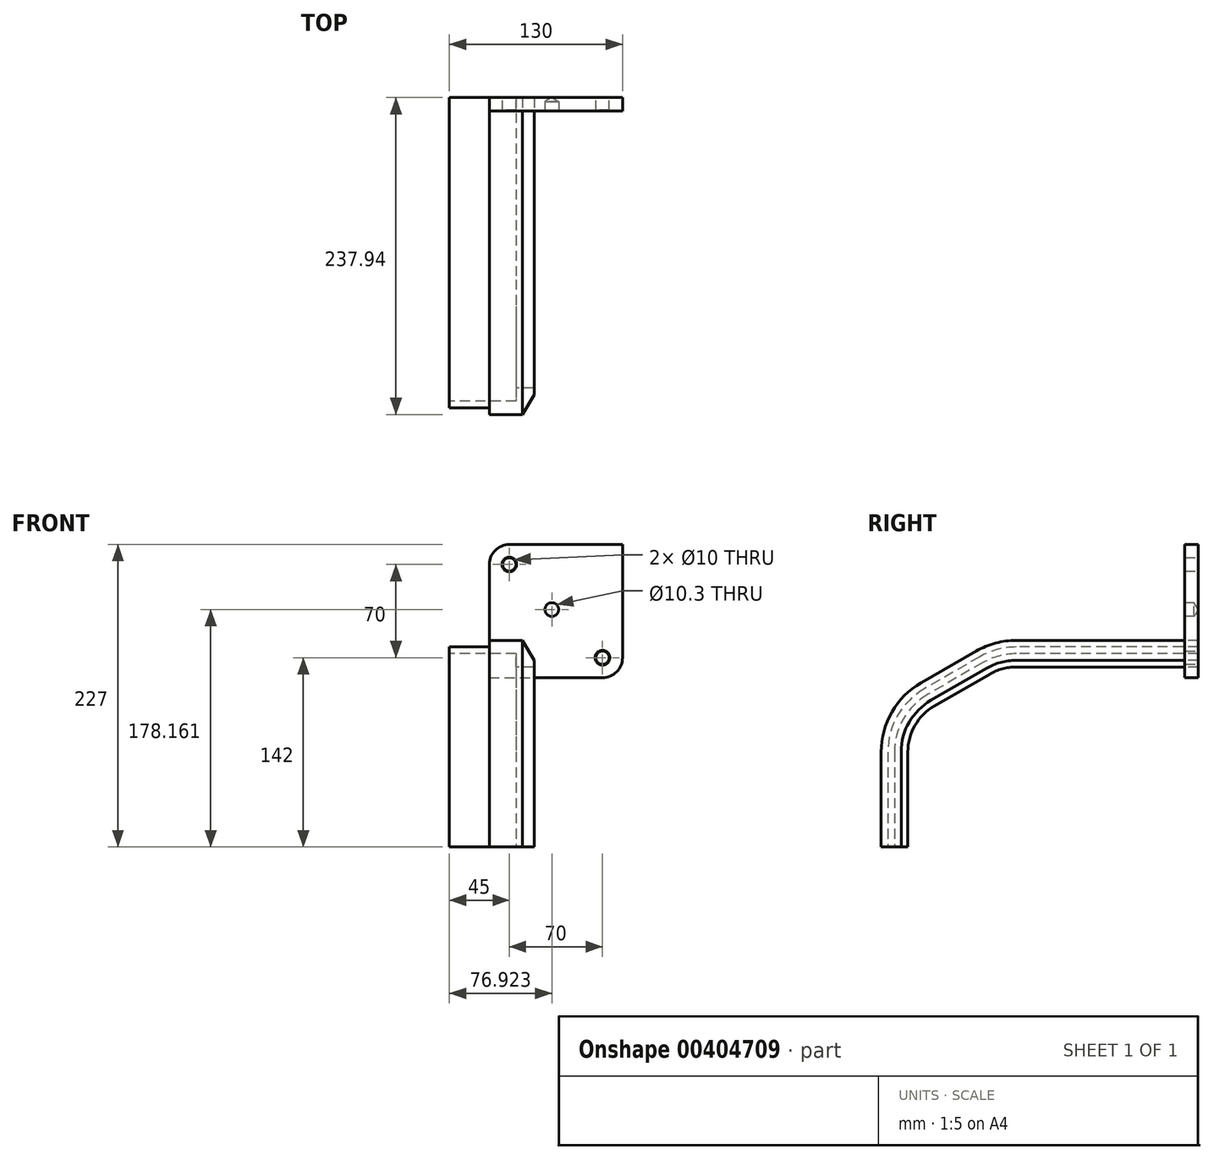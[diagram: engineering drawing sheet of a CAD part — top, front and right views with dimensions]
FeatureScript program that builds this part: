
annotation { "Feature Type Name" : "Feature", "Feature Type Description" : "" }
export const myFeature = defineFeature(function(context is Context, id is Id, definition is map)
    precondition{}
    {
        {
            var Q0;
            Q0=qCreatedBy(makeId("Front.planeOp"),FACE);
            var sketch = newSketch(context, id + "F0", { "sketchPlane" : qUnion([Q0])});
            skLineSegment(sketch, "E0.bottom", {"start": v(0, 0) * mm, "end": v(85, 0) * mm});
            skLineSegment(sketch, "E0.top", {"start": v(15, 100) * mm, "end": v(100, 100) * mm});
            skLineSegment(sketch, "E0.left", {"start": v(0, 0) * mm, "end": v(0, 85) * mm});
            skLineSegment(sketch, "E0.right", {"start": v(100, 15) * mm, "end": v(100, 100) * mm});
            skPoint(sketch, "E1.visualSharp", {"position": v(0, 100) * mm});
            skArc(sketch, "E1.filletArc", {"start": v(15, 100) * mm, "mid": v(4.4, 95.6) * mm, "end": v(0, 85) * mm});
            skPoint(sketch, "E2.visualSharp", {"position": v(100, 0) * mm});
            skArc(sketch, "E2.filletArc", {"start": v(85, 0) * mm, "mid": v(95.6, 4.4) * mm, "end": v(100, 15) * mm});
            skCircle(sketch, "E3", {"center": v(15, 85) * mm, "radius": 5 * mm});
            skCircle(sketch, "E4", {"center": v(85, 15) * mm, "radius": 5 * mm});
            skSolve(sketch);
        }
        {
            var Q0;
            Q0=makeQuery(id+"F0.imprint","IMPRINT",FACE,{"disambiguationData":[TD([[makeQuery(id+"F0.imprint","IMPRINT",EDGE,{"derivedFrom":sQuery(id+"F0.wireOp",EDGE,"E0.bottom")}),1.0]])]});
            extrude(context, id + "F1", {"entities" : qUnion([Q0]), "depth" : 10 * mm});
        }
        {
            var Q0;
            Q0=makeQuery(id+"F1.opExtrude","CAP_FACE",FACE,{"disambiguationData":[OSD([sQuery(id+"F0.wireOp",EDGE,"E0.bottom"),sQuery(id+"F0.wireOp",EDGE,"E0.top"),sQuery(id+"F0.wireOp",EDGE,"E0.left"),sQuery(id+"F0.wireOp",EDGE,"E0.right"),sQuery(id+"F0.wireOp",EDGE,"E1.filletArc"),sQuery(id+"F0.wireOp",EDGE,"E2.filletArc"),sQuery(id+"F0.wireOp",EDGE,"E3"),sQuery(id+"F0.wireOp",EDGE,"E4")])],"isStart":false});
            var sketch = newSketch(context, id + "F2", { "sketchPlane" : qUnion([Q0])});
            skPoint(sketch, "E5", {"position": v(46.92, 51.16) * mm});
            skSolve(sketch);
        }
        {
            var Q0;
            Q0=sQuery(id+"F2.wireOp",VERTEX,"E5");
            var Q1;
            Q1=makeQuery(id+"F1.opExtrude","SWEPT_BODY",BODY,{"disambiguationData":[OSD([sQuery(id+"F0.wireOp",EDGE,"E0.bottom"),sQuery(id+"F0.wireOp",EDGE,"E0.top"),sQuery(id+"F0.wireOp",EDGE,"E0.left"),sQuery(id+"F0.wireOp",EDGE,"E0.right"),sQuery(id+"F0.wireOp",EDGE,"E1.filletArc"),sQuery(id+"F0.wireOp",EDGE,"E2.filletArc"),sQuery(id+"F0.wireOp",EDGE,"E3"),sQuery(id+"F0.wireOp",EDGE,"E4")])]});
            hole(context, id + "F3", {"style" : HoleStyle.SIMPLE, "endStyle" : HoleEndStyle.BLIND, "standardTappedOrClearance" : lookupTablePath({ "standard" : "ISO", "engagement" : "75%", "pitch" : "1.75 mm", "size" : "M12", "type" : "Tapped" }), "standardBlindInLast" : lookupTablePath({ "standard" : "ISO", "engagement" : "75%", "pitch" : "1.75 mm", "size" : "M12", "type" : "Tapped" }), "holeDiameter" : 10.3 * mm, "showTappedDepth" : true, "holeDepth" : 7 * mm, "isTappedThrough" : true, "tappedDepth" : 1.75 * mm, "tapClearance" : 3, "locations" : qUnion([Q0]), "scope" : qUnion([Q1]), "majorDiameter" : 12 * mm});
        }
        {
            var Q0;
            Q0=makeQuery(id+"F3.hole-0.boolean.opBoolean","COPY",EDGE,{"derivedFrom":makeQuery(id+"F3.hole-0.opRevolve","SWEPT_EDGE",EDGE,{"disambiguationData":[OSD([sQuery(id+"F3.hole-0.sketch.wireOp",EDGE,"core_line_2"),sQuery(id+"F3.hole-0.sketch.wireOp",EDGE,"core_line_3")])]})});
            var Q1;
            Q1=makeQuery(id+"F1.opExtrude","CAP_EDGE",EDGE,{"disambiguationData":[OSD([sQuery(id+"F0.wireOp",EDGE,"E3")])],"isStart":false});
            var Q2;
            Q2=makeQuery(id+"F1.opExtrude","CAP_EDGE",EDGE,{"disambiguationData":[OSD([sQuery(id+"F0.wireOp",EDGE,"E4")])],"isStart":false});
            chamfer(context, id + "F4", {"entities" : qUnion([Q0, Q1, Q2]), "width" : 0.5 * mm, "tangentPropagation" : true});
        }
        {
            var Q0;
            Q0=qCreatedBy(makeId("Front.planeOp"),FACE);
            var sketch = newSketch(context, id + "F5", { "sketchPlane" : qUnion([Q0])});
            skLineSegment(sketch, "E6", {"start": v(-30, 18) * mm, "end": v(-30, 23) * mm});
            skLineSegment(sketch, "E7", {"start": v(-30, 23) * mm, "end": v(0, 23) * mm});
            skLineSegment(sketch, "E8", {"start": v(0, 23) * mm, "end": v(0, 28) * mm});
            skLineSegment(sketch, "E9", {"start": v(0, 28) * mm, "end": v(25, 28) * mm});
            skLineSegment(sketch, "E10", {"start": v(25, 28) * mm, "end": v(33.66, 13) * mm});
            skLineSegment(sketch, "E11", {"start": v(33.66, 13) * mm, "end": v(33.66, 8) * mm});
            skLineSegment(sketch, "E12", {"start": v(33.66, 8) * mm, "end": v(20, 8) * mm});
            skLineSegment(sketch, "E13", {"start": v(20, 8) * mm, "end": v(20, 18) * mm});
            skLineSegment(sketch, "E14", {"start": v(20, 18) * mm, "end": v(-30, 18) * mm});
            skLineSegment(sketch, "E15", {"start": v(0, 0) * mm, "end": v(-60.46, 0) * mm, "construction": true});
            skSolve(sketch);
        }
        {
            var Q0;
            Q0=qCreatedBy(makeId("Right.planeOp"),FACE);
            var sketch = newSketch(context, id + "F6", { "sketchPlane" : qUnion([Q0])});
            skPoint(sketch, "E16.0", {"position": v(0, 18) * mm});
            skLineSegment(sketch, "E17", {"start": v(0, 18) * mm, "end": v(-136.6, 18) * mm});
            skLineSegment(sketch, "E18", {"start": v(-161.6, 11.3) * mm, "end": v(-202.94, -12.57) * mm});
            skLineSegment(sketch, "E19", {"start": v(-227.94, -55.87) * mm, "end": v(-227.94, -127) * mm});
            skPoint(sketch, "E20.visualSharp", {"position": v(-150, 18) * mm});
            skArc(sketch, "E20.filletArc", {"start": v(-136.6, 18) * mm, "mid": v(-149.54, 16.3) * mm, "end": v(-161.6, 11.3) * mm});
            skPoint(sketch, "E21.visualSharp", {"position": v(-227.94, -27) * mm});
            skArc(sketch, "E21.filletArc", {"start": v(-202.94, -12.57) * mm, "mid": v(-221.24, -30.87) * mm, "end": v(-227.94, -55.87) * mm});
            skSolve(sketch);
        }
        {
            var Q0;
            Q0=makeQuery(id+"F5.imprint","IMPRINT",FACE,{"disambiguationData":[TD([[makeQuery(id+"F5.imprint","IMPRINT",EDGE,{"derivedFrom":sQuery(id+"F5.wireOp",EDGE,"E6")}),-1.0]])]});
            var Q1;
            Q1=sQuery(id+"F6.wireOp",EDGE,"E17");
            var Q2;
            Q2=sQuery(id+"F6.wireOp",EDGE,"E20.filletArc");
            var Q3;
            Q3=sQuery(id+"F6.wireOp",EDGE,"E18");
            var Q4;
            Q4=sQuery(id+"F6.wireOp",EDGE,"E21.filletArc");
            var Q5;
            Q5=sQuery(id+"F6.wireOp",EDGE,"E19");
            sweep(context, id + "F7", {"profiles" : qUnion([Q0]), "path" : qUnion([Q1, Q2, Q3, Q4, Q5])});
        }
    });
